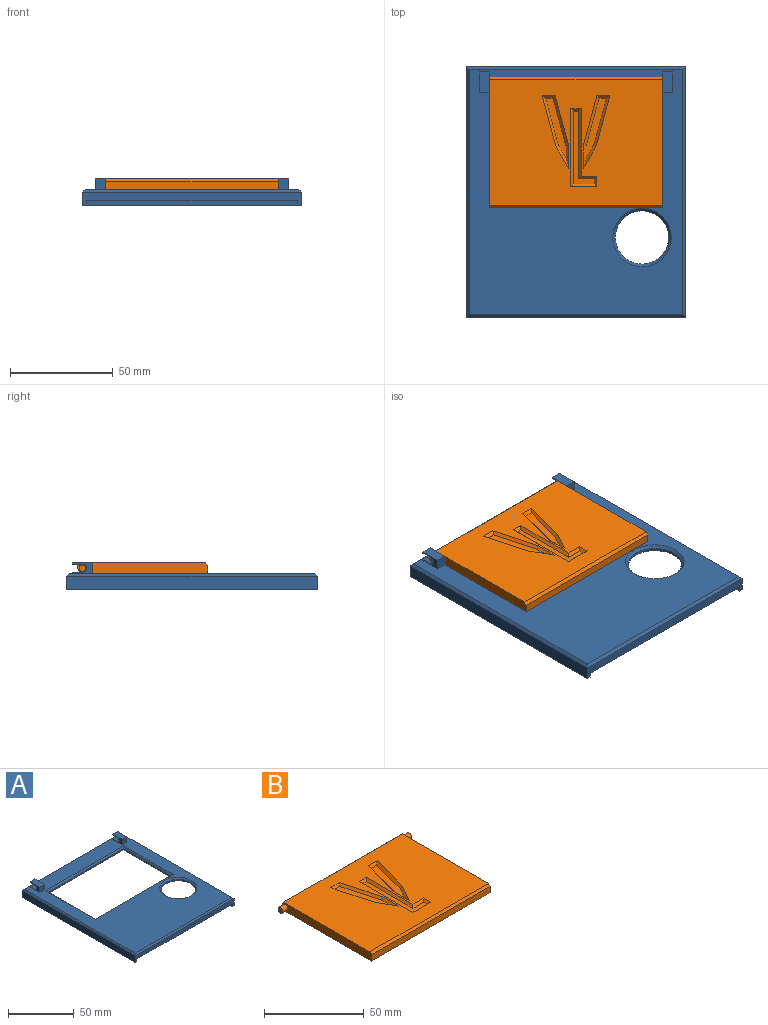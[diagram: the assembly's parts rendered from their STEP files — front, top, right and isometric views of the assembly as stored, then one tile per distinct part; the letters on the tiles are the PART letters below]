
ASSEMBLY  parts=2 mates=1
PART A: 43 faces, bbox 106.7x121.9x12.7 mm
  f0: plane 5.08x0.64mm, normal (0,1,0), area 3.2mm2, adj f2,f4,f30,f40
  f1: plane 5.08x0.64mm, normal (0,1,0), area 3.2mm2, adj f3,f34,f36,f37
  f2: plane 10.16x5.08mm, normal (-1,0,0), area 26.6mm2, adj f0,f4,f29,f31,f32,f40,f41,f42
  f3: plane 10.16x5.08mm, normal (1,0,0), area 26.6mm2, adj f1,f4,f33,f35,f36,f37,f38,f39
  f4: plane 119.38x104.14mm, normal (0,0,1), area 7212mm2, adj f0,f2,f3,f20,f21,f22,f23,f24
  f5: plane 119.16x5.08mm, normal (1,0,0), area 601.6mm2, adj f6,f11,f12,f18,f19
  f6: plane 102.62x5.08mm, normal (0,-1,0), area 521.3mm2, adj f5,f7,f12,f18
  f7: plane 119.16x5.08mm, normal (-1,0,0), area 601.6mm2, adj f6,f11,f12,f18,f19
  f8: plane 121.92x6.35mm, normal (1,0,0), area 774.2mm2, adj f9,f11,f12,f25
  f9: plane 106.68x6.35mm, normal (0,1,0), area 677.4mm2, adj f8,f10,f12,f26
  f10: plane 121.92x6.35mm, normal (-1,0,0), area 774.2mm2, adj f9,f11,f12,f28
  f11: plane 106.68x6.35mm, normal (0,-1,0), area 438.9mm2, adj f5,f7,f8,f10,f12,f19,f27
  f12: plane 121.92x106.68mm, normal (0,0,-1), area 778.3mm2, adj f5,f6,f7,f8,f9,f10,f11
  f13: plane 50.88x1.27mm, normal (1,0,0), area 64.6mm2, adj f14,f16,f18,f21
  f14: plane 81.36x1.27mm, normal (0,-1,0), area 103.3mm2, adj f13,f15,f18,f22
  f15: plane 50.88x1.27mm, normal (-1,0,0), area 64.6mm2, adj f14,f16,f18,f24
  f16: plane 81.36x1.27mm, normal (0,1,0), area 103.3mm2, adj f13,f15,f18,f23
  f17: cylinder r=12.95mm len=25.91mm, axis (0,0,-1), area 103.4mm2, adj f18,f20
  f18: plane 116.41x102.62mm, normal (0,0,-1), area 7279.1mm2, adj f5,f6,f7,f13,f14,f15,f16,f17
  f19: plane 102.62x2.76mm, normal (0,0.71,-0.71), area 399.9mm2, adj f5,f7,f11,f18
  f20: cone r=12.95mm half-angle=45deg, axis (0,0,1), area 153.4mm2, adj f4,f17
  f21: plane 53.42x1.27mm, normal (0.71,0,0.71), area 93.7mm2, adj f4,f13,f22,f23
  f22: plane 83.9x1.27mm, normal (0,-0.71,0.71), area 148.4mm2, adj f4,f14,f21,f24
  f23: plane 83.9x1.27mm, normal (0,0.71,0.71), area 148.4mm2, adj f4,f16,f21,f24
  f24: plane 53.42x1.27mm, normal (-0.71,0,0.71), area 93.7mm2, adj f4,f15,f22,f23
  f25: plane 121.92x1.27mm, normal (0.71,0,0.71), area 216.7mm2, adj f4,f8,f26,f27
  f26: plane 106.68x1.27mm, normal (0,0.71,0.71), area 189.3mm2, adj f4,f9,f25,f28
  f27: plane 106.68x1.27mm, normal (0,-0.71,0.71), area 189.3mm2, adj f4,f11,f25,f28
  f28: plane 121.92x1.27mm, normal (-0.71,0,0.71), area 216.7mm2, adj f4,f10,f26,f27
  f29: plane 5.08x5.08mm, normal (0,-1,0), area 25.8mm2, adj f2,f4,f30,f32
  f30: plane 10.16x5.08mm, normal (1,0,0), area 26.6mm2, adj f0,f4,f29,f31,f32,f40,f41,f42
  f31: plane 5.08x0.64mm, normal (0,1,0), area 3.2mm2, adj f2,f30,f32,f42
  f32: plane 10.16x5.08mm, normal (0,0,1), area 51.6mm2, adj f2,f29,f30,f31
  f33: plane 5.08x0.64mm, normal (0,1,0), area 3.2mm2, adj f3,f4,f34,f39
  f34: plane 10.16x5.08mm, normal (-1,0,0), area 26.6mm2, adj f1,f4,f33,f35,f36,f37,f38,f39
  f35: plane 5.08x5.08mm, normal (0,-1,0), area 25.8mm2, adj f3,f4,f34,f36
  f36: plane 10.16x5.08mm, normal (0,0,1), area 51.6mm2, adj f1,f3,f34,f35
  f37: plane 5.08x5.08mm, normal (0,0,-1), area 25.8mm2, adj f1,f3,f34,f38
  f38: cylinder r=1.91mm len=5.08mm, axis (1,0,0), area 30.4mm2, adj f3,f34,f37,f39
  f39: plane 5.08x5.08mm, normal (0,0,1), area 25.8mm2, adj f3,f33,f34,f38
  f40: plane 5.08x5.08mm, normal (0,0,1), area 25.8mm2, adj f0,f2,f30,f41
  f41: cylinder r=1.91mm len=5.08mm, axis (1,0,0), area 30.4mm2, adj f2,f30,f40,f42
  f42: plane 5.08x5.08mm, normal (0,0,-1), area 25.8mm2, adj f2,f30,f31,f41
PART B: 36 faces, bbox 91.4x63.5x5.1 mm
  f0: plane 83.82x60.96mm, normal (0,0,1), area 4496mm2, adj f1,f7,f15,f16,f20,f21,f22,f23
  f1: plane 63.5x5.08mm, normal (-1,0,0), area 309.3mm2, adj f0,f2,f8,f10,f14,f15,f16
  f2: plane 83.82x3.81mm, normal (0,-1,0), area 319.4mm2, adj f1,f7,f8,f15
  f3: plane 58.42x2.54mm, normal (1,0,0), area 148.3mm2, adj f4,f6,f8,f9,f14
  f4: plane 78.74x2.32mm, normal (0,-1,0), area 182.8mm2, adj f3,f5,f9,f14
  f5: plane 58.42x2.54mm, normal (-1,0,0), area 148.3mm2, adj f4,f6,f8,f9,f14
  f6: plane 78.74x2.54mm, normal (0,1,0), area 200mm2, adj f3,f5,f8,f9
  f7: plane 63.5x5.08mm, normal (1,0,0), area 309.3mm2, adj f0,f2,f8,f12,f14,f15,f16
  f8: plane 83.82x59.69mm, normal (0,0,-1), area 503.2mm2, adj f1,f2,f3,f5,f6,f7,f14
  f9: plane 78.74x58.42mm, normal (0,0,-1), area 4600mm2, adj f3,f4,f5,f6
  f10: cylinder r=1.65mm len=3.81mm, axis (1,0,0), area 39.5mm2, adj f1,f11
  f11: plane 3.3x3.3mm, normal (-1,0,0), area 8.6mm2, adj f10
  f12: cylinder r=1.65mm len=3.81mm, axis (-1,0,0), area 39.5mm2, adj f7,f13
  f13: plane 3.3x3.3mm, normal (1,0,0), area 8.6mm2, adj f12
  f14: cylinder r=3.81mm len=83.82mm, axis (-1,0,0), area 399.7mm2, adj f1,f3,f4,f5,f7,f8,f16
  f15: plane 83.82x1.27mm, normal (0,-0.71,0.71), area 150.5mm2, adj f0,f1,f2,f7
  f16: plane 83.82x1.27mm, normal (0,0.71,0.71), area 150.5mm2, adj f0,f1,f7,f14
  f17: plane 35.56x10.16mm, normal (0,0,1), area 109.7mm2, adj f30,f31,f32,f33,f34,f35
  f18: plane 29.52x10mm, normal (0,0,1), area 97.8mm2, adj f25,f26,f27,f28,f29
  f19: plane 29.52x10mm, normal (0,0,1), area 97.8mm2, adj f20,f21,f22,f23,f24
  f20: plane 6.35x1.27mm, normal (0,-0.71,0.71), area 9mm2, adj f0,f19,f21,f22
  f21: plane 24.53x7.76mm, normal (-0.68,0.18,0.71), area 44mm2, adj f0,f19,f20,f23
  f22: plane 24.7x7.55mm, normal (0.68,-0.18,0.71), area 44.6mm2, adj f0,f19,f20,f24
  f23: plane 11.49x6.35mm, normal (-0.61,0.35,0.71), area 18.4mm2, adj f0,f19,f21,f24
  f24: plane 11x1.27mm, normal (0.71,0,0.71), area 15.3mm2, adj f0,f19,f22,f23
  f25: plane 24.53x7.76mm, normal (0.68,0.18,0.71), area 44mm2, adj f0,f18,f26,f27
  f26: plane 6.35x1.27mm, normal (0,-0.71,0.71), area 9mm2, adj f0,f18,f25,f28
  f27: plane 11.49x6.35mm, normal (0.61,0.35,0.71), area 18.4mm2, adj f0,f18,f25,f29
  f28: plane 24.7x7.55mm, normal (-0.68,-0.18,0.71), area 44.6mm2, adj f0,f18,f26,f29
  f29: plane 11x1.27mm, normal (-0.71,0,0.71), area 15.3mm2, adj f0,f18,f27,f28
  f30: plane 38.1x1.27mm, normal (0.71,0,0.71), area 66.1mm2, adj f0,f17,f31,f32
  f31: plane 5.08x1.27mm, normal (0,-0.71,0.71), area 6.8mm2, adj f0,f17,f30,f33
  f32: plane 12.7x1.27mm, normal (0,0.71,0.71), area 20.5mm2, adj f0,f17,f30,f34
  f33: plane 34.29x1.27mm, normal (-0.71,0,0.71), area 59.3mm2, adj f0,f17,f31,f35
  f34: plane 5.08x1.27mm, normal (-0.71,0,0.71), area 6.8mm2, adj f0,f17,f32,f35
  f35: plane 8.89x1.27mm, normal (0,-0.71,0.71), area 13.7mm2, adj f0,f17,f33,f34
PLACE A t=(2.29,-3.16,-6.73)mm fixed
PLACE B t=(2.29,20.97,0.89)mm
MATE revolute B.f10 <-> A.f38  axis (1,0,0) through (-39.62,50.18,3.43)mm
